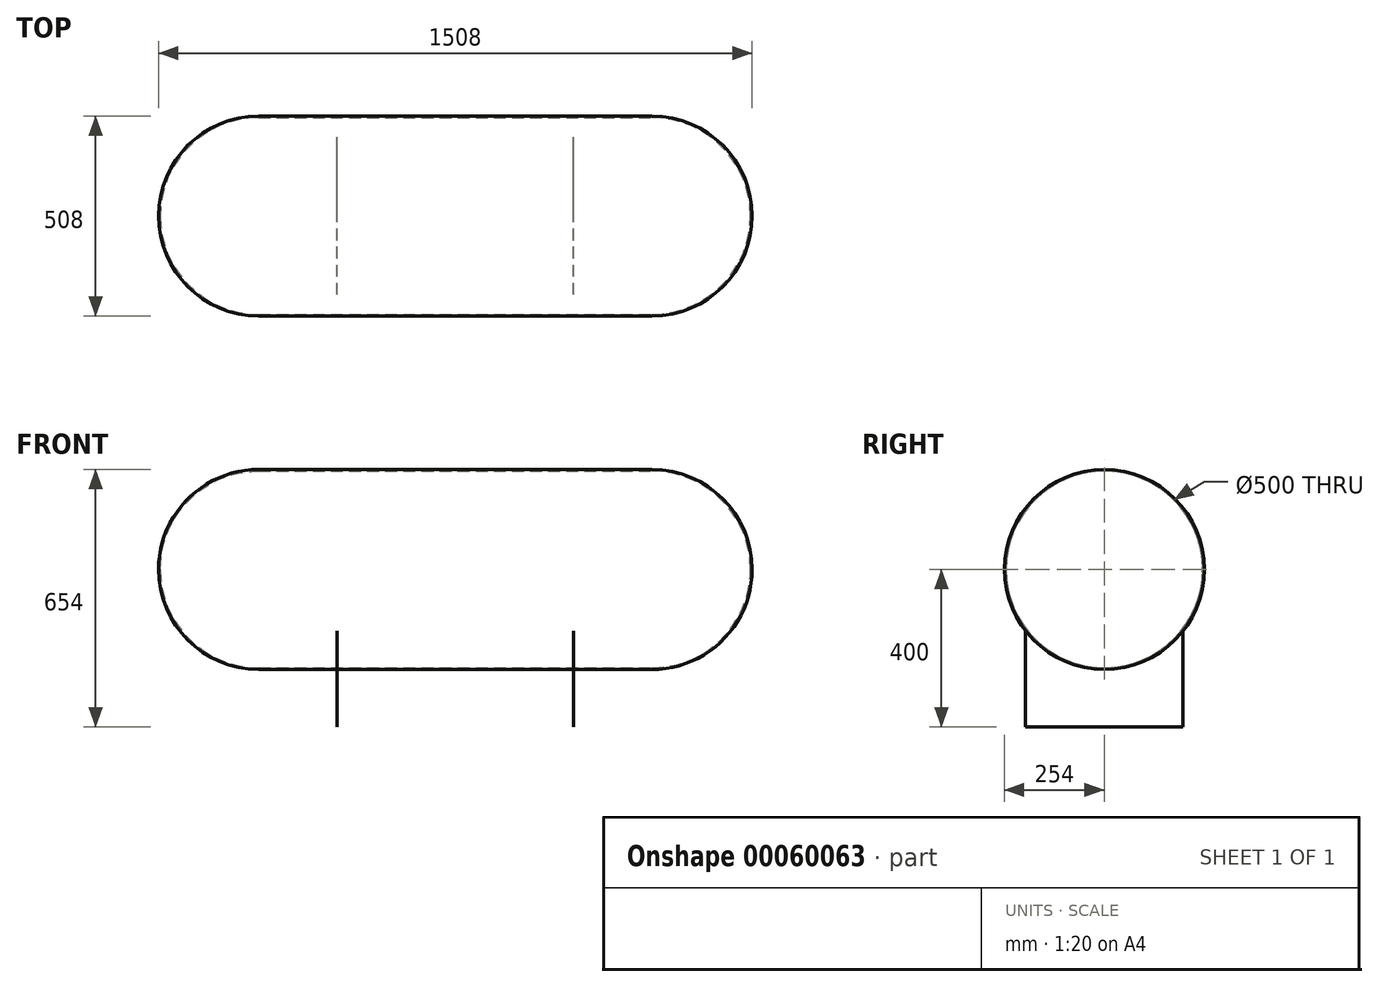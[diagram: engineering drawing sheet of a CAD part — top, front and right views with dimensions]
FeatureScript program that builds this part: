
annotation { "Feature Type Name" : "Feature", "Feature Type Description" : "" }
export const myFeature = defineFeature(function(context is Context, id is Id, definition is map)
    precondition{}
    {
        {
            var Q0;
            Q0=qCreatedBy(makeId("Front.planeOp"),FACE);
            var sketch = newSketch(context, id + "F0", { "sketchPlane" : qUnion([Q0])});
            skLineSegment(sketch, "E0", {"start": v(0, 0) * mm, "end": v(-500, 0) * mm, "construction": true});
            skArc(sketch, "E1", {"start": v(-750, 0) * mm, "mid": v(-676.78, 176.78) * mm, "end": v(-500, 250) * mm});
            skLineSegment(sketch, "E2", {"start": v(-500, 250) * mm, "end": v(0, 250) * mm});
            skLineSegment(sketch, "E3.MirrorCS", {"start": v(500, 250) * mm, "end": v(0, 250) * mm});
            skArc(sketch, "E4.MirrorCS", {"start": v(750, 0) * mm, "mid": v(676.78, 176.78) * mm, "end": v(500, 250) * mm});
            skArc(sketch, "E5.0", {"start": v(754, 0) * mm, "mid": v(679.6, 179.6) * mm, "end": v(500, 254) * mm});
            skLineSegment(sketch, "E5.1", {"start": v(500, 254) * mm, "end": v(0, 254) * mm});
            skLineSegment(sketch, "E5.2", {"start": v(-500, 254) * mm, "end": v(0, 254) * mm});
            skArc(sketch, "E5.3", {"start": v(-754, 0) * mm, "mid": v(-679.6, 179.6) * mm, "end": v(-500, 254) * mm});
            skLineSegment(sketch, "E6", {"start": v(-754, 0) * mm, "end": v(-750, 0) * mm});
            skLineSegment(sketch, "E7", {"start": v(750, 0) * mm, "end": v(754, 0) * mm});
            skSolve(sketch);
        }
        {
            var Q0;
            Q0 = qSketchRegion(id + "F0", true);
            var Q1;
            Q1=sQuery(id+"F0.wireOp",EDGE,"E0");
            revolve(context, id + "F1", {"entities" : qUnion([Q0]), "axis" : qUnion([Q1]), "revolveType" : RevolveType.FULL});
        }
        {
            var Q0;
            Q0=qCreatedBy(makeId("Right.planeOp"),FACE);
            cPlane(context, id + "F2", {"entities" : qUnion([Q0]), "cplaneType" : CPlaneType.OFFSET, "offset" : 300 * mm, "width" : 150 * mm, "height" : 150 * mm});
        }
        {
            var Q0;
            Q0=qCreatedBy(id+"F2.planeOp",FACE);
            var sketch = newSketch(context, id + "F3", { "sketchPlane" : qUnion([Q0])});
            skArc(sketch, "E8.0", {"start": v(-200, -156.58) * mm, "mid": v(0, -254) * mm, "end": v(200, -156.58) * mm});
            skLineSegment(sketch, "E9", {"start": v(-200, -156.58) * mm, "end": v(-200, -400) * mm});
            skLineSegment(sketch, "E10", {"start": v(-200, -400) * mm, "end": v(200, -400) * mm});
            skLineSegment(sketch, "E11", {"start": v(200, -400) * mm, "end": v(200, -156.58) * mm});
            skLineSegment(sketch, "E12", {"start": v(0, -400) * mm, "end": v(0, 0) * mm, "construction": true});
            skSolve(sketch);
        }
        {
            var Q0;
            Q0=makeQuery(id+"F3.imprint","IMPRINT",FACE,{"disambiguationData":[TD([[makeQuery(id+"F3.imprint","IMPRINT",EDGE,{"derivedFrom":sQuery(id+"F3.wireOp",EDGE,"E8.0")}),-1.0]])]});
            extrude(context, id + "F4", {"entities" : qUnion([Q0]), "depth" : 3 / 101.6 * mm});
        }
        {
            var Q0;
            Q0=makeQuery(id+"F4.opExtrude","SWEPT_BODY",BODY,{"disambiguationData":[OSD([sQuery(id+"F3.wireOp",EDGE,"E8.0"),sQuery(id+"F3.wireOp",EDGE,"E9"),sQuery(id+"F3.wireOp",EDGE,"E10"),sQuery(id+"F3.wireOp",EDGE,"E11")])]});
            var Q1;
            Q1=qCreatedBy(makeId("Right.planeOp"),FACE);
            mirror(context, id + "F5", {"operationType" : NewBodyOperationType.ADD, "entities" : qUnion([Q0]), "mirrorPlane" : qUnion([Q1])});
        }
    });
